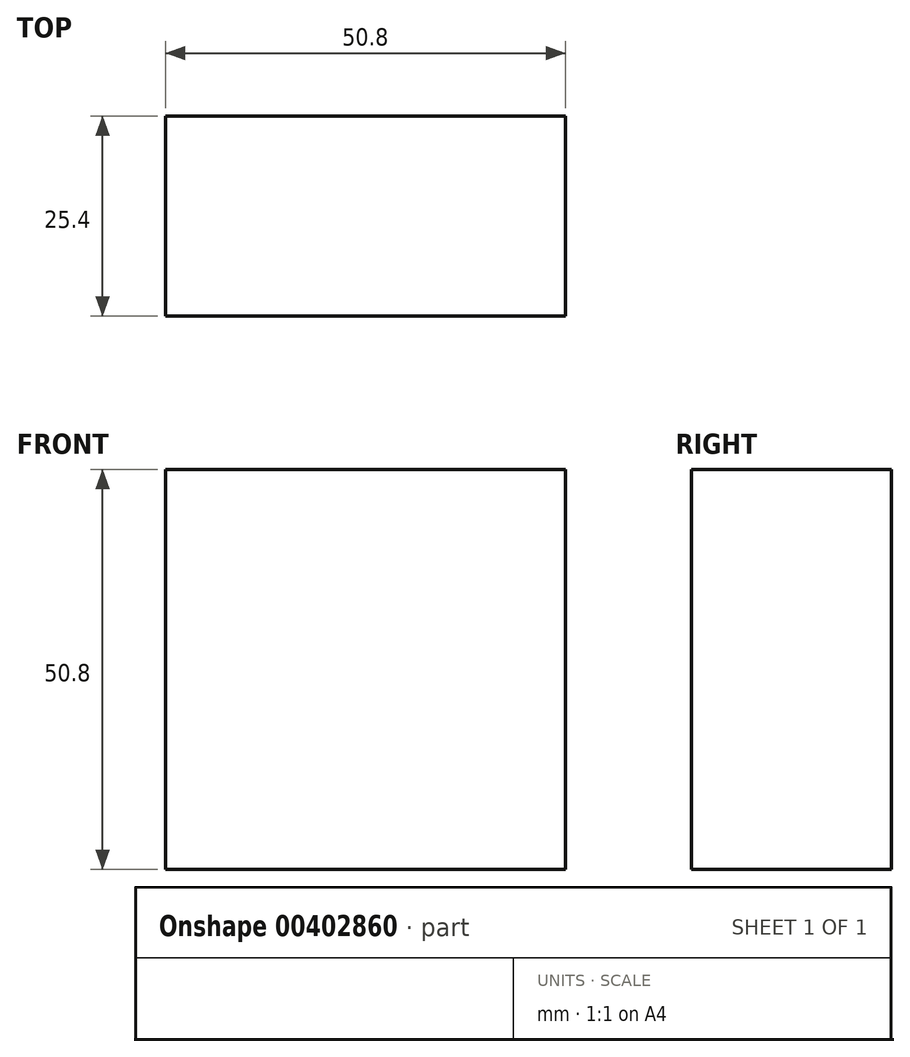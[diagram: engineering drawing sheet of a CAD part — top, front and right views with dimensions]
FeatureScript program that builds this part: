
annotation { "Feature Type Name" : "Feature", "Feature Type Description" : "" }
export const myFeature = defineFeature(function(context is Context, id is Id, definition is map)
    precondition{}
    {
        {
            var Q0;
            Q0=qCreatedBy(makeId("Front.planeOp"),FACE);
            var sketch = newSketch(context, id + "F0", { "sketchPlane" : qUnion([Q0])});
            skLineSegment(sketch, "E0.bottom", {"start": v(0, 0) * mm, "end": v(-50.8, 0) * mm});
            skLineSegment(sketch, "E0.top", {"start": v(0, 50.8) * mm, "end": v(-50.8, 50.8) * mm});
            skLineSegment(sketch, "E0.left", {"start": v(0, 0) * mm, "end": v(0, 50.8) * mm});
            skLineSegment(sketch, "E0.right", {"start": v(-50.8, 0) * mm, "end": v(-50.8, 50.8) * mm});
            skSolve(sketch);
        }
        {
            var Q0;
            Q0=makeQuery(id+"F0.imprint","IMPRINT",FACE,{"disambiguationData":[TD([[makeQuery(id+"F0.imprint","IMPRINT",EDGE,{"derivedFrom":sQuery(id+"F0.wireOp",EDGE,"E0.bottom")}),-1.0]])]});
            extrude(context, id + "F1", {"entities" : qUnion([Q0]), "depth" : 25.4 * mm});
        }
    });
